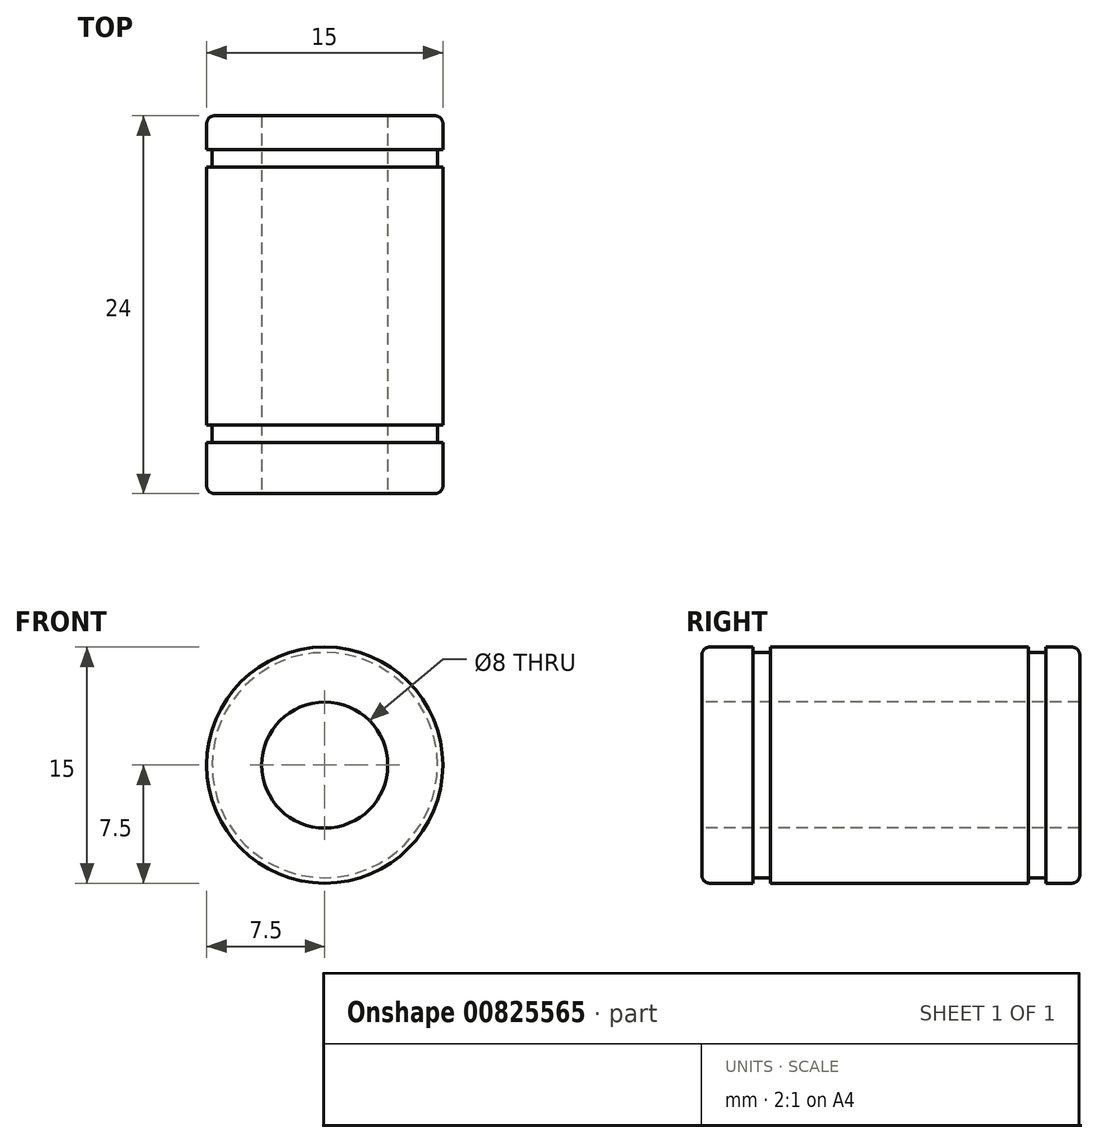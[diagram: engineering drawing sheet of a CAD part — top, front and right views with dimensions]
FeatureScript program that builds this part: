
annotation { "Feature Type Name" : "Feature", "Feature Type Description" : "" }
export const myFeature = defineFeature(function(context is Context, id is Id, definition is map)
    precondition{}
    {
        {
            var Q0;
            Q0=qCreatedBy(makeId("Right.planeOp"),FACE);
            var sketch = newSketch(context, id + "F0", { "sketchPlane" : qUnion([Q0])});
            skLineSegment(sketch, "E0.bottom", {"start": v(-12, 7.5) * mm, "end": v(12, 7.5) * mm});
            skLineSegment(sketch, "E0.top", {"start": v(-12, 4) * mm, "end": v(12, 4) * mm});
            skLineSegment(sketch, "E0.left", {"start": v(-12, 7.5) * mm, "end": v(-12, 4) * mm});
            skLineSegment(sketch, "E0.right", {"start": v(12, 7.5) * mm, "end": v(12, 4) * mm});
            skLineSegment(sketch, "E1", {"start": v(-17.94, 0) * mm, "end": v(22.06, 0) * mm, "construction": true});
            skLineSegment(sketch, "E2.bottom", {"start": v(8.75, 7.5) * mm, "end": v(9.85, 7.5) * mm});
            skLineSegment(sketch, "E2.top", {"start": v(8.75, 7.15) * mm, "end": v(9.85, 7.15) * mm});
            skLineSegment(sketch, "E2.left", {"start": v(9.85, 7.5) * mm, "end": v(9.85, 7.15) * mm});
            skLineSegment(sketch, "E2.right", {"start": v(8.75, 7.5) * mm, "end": v(8.75, 7.15) * mm});
            skLineSegment(sketch, "E3.bottom", {"start": v(-8.75, 7.5) * mm, "end": v(-7.65, 7.5) * mm});
            skLineSegment(sketch, "E3.top", {"start": v(-8.75, 7.15) * mm, "end": v(-7.65, 7.15) * mm});
            skLineSegment(sketch, "E3.left", {"start": v(-8.75, 7.5) * mm, "end": v(-8.75, 7.15) * mm});
            skLineSegment(sketch, "E3.right", {"start": v(-7.65, 7.5) * mm, "end": v(-7.65, 7.15) * mm});
            skLineSegment(sketch, "E4", {"start": v(-8.75, 7.15) * mm, "end": v(8.75, 7.15) * mm, "construction": true});
            skLineSegment(sketch, "E5", {"start": v(0, 0) * mm, "end": v(0, 7.15) * mm, "construction": true});
            skLineSegment(sketch, "E6", {"start": v(0, 0) * mm, "end": v(0, 4) * mm, "construction": true});
            skSolve(sketch);
        }
        {
            var Q0;
            Q0=makeQuery(id+"F0.imprint","IMPRINT",FACE,{"disambiguationData":[TD([[makeQuery(id+"F0.imprint","IMPRINT",EDGE,{"derivedFrom":sQuery(id+"F0.wireOp",EDGE,"E0.top")}),1.0]])]});
            var Q1;
            Q1=sQuery(id+"F0.wireOp",EDGE,"E1");
            revolve(context, id + "F1", {"entities" : qUnion([Q0]), "axis" : qUnion([Q1]), "revolveType" : RevolveType.FULL});
        }
        {
            var Q0;
            Q0=makeQuery(id+"F1.opRevolve","SWEPT_EDGE",EDGE,{"disambiguationData":[OSD([sQuery(id+"F0.wireOp",EDGE,"E0.bottom"),sQuery(id+"F0.wireOp",EDGE,"E0.right")])]});
            var Q1;
            Q1=makeQuery(id+"F1.opRevolve","SWEPT_EDGE",EDGE,{"disambiguationData":[OSD([sQuery(id+"F0.wireOp",EDGE,"E0.bottom"),sQuery(id+"F0.wireOp",EDGE,"E0.left")])]});
            fillet(context, id + "F2", {"entities" : qUnion([Q0, Q1]), "radius" : 0.5 * mm, "tangentPropagation" : true, "allowEdgeOverflow" : false});
        }
    });
